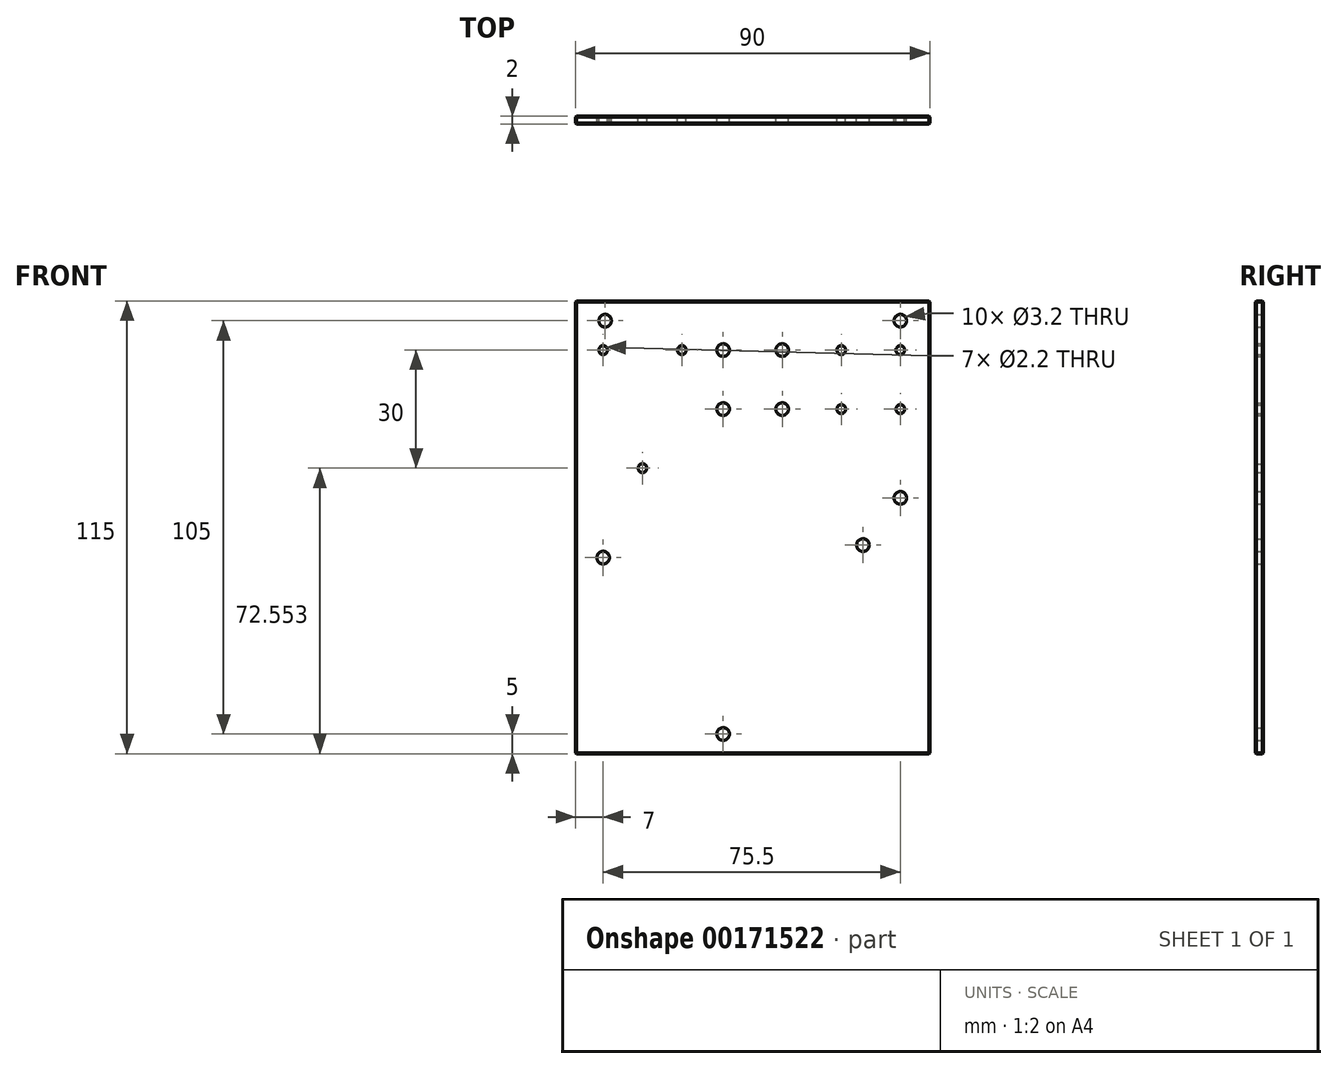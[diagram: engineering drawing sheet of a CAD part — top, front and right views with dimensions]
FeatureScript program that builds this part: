
annotation { "Feature Type Name" : "Feature", "Feature Type Description" : "" }
export const myFeature = defineFeature(function(context is Context, id is Id, definition is map)
    precondition{}
    {
        {
            var Q0;
            Q0=qCreatedBy(makeId("Front.planeOp"),FACE);
            var sketch = newSketch(context, id + "F0", { "sketchPlane" : qUnion([Q0])});
            skLineSegment(sketch, "E0.bottom", {"start": v(45, -57.5) * mm, "end": v(-45, -57.5) * mm});
            skLineSegment(sketch, "E0.top", {"start": v(45, 57.5) * mm, "end": v(-45, 57.5) * mm});
            skLineSegment(sketch, "E0.left", {"start": v(45, -57.5) * mm, "end": v(45, 57.5) * mm});
            skLineSegment(sketch, "E0.right", {"start": v(-45, -57.5) * mm, "end": v(-45, 57.5) * mm});
            skPoint(sketch, "E0.middle", {"position": v(0, 0) * mm});
            skCircle(sketch, "E1", {"center": v(-37.5, 52.5) * mm, "radius": 1.6 * mm});
            skCircle(sketch, "E2", {"center": v(37.5, 52.5) * mm, "radius": 1.6 * mm});
            skCircle(sketch, "E3", {"center": v(37.5, 7.5) * mm, "radius": 1.6 * mm});
            skCircle(sketch, "E4", {"center": v(-7.5, -52.5) * mm, "radius": 1.6 * mm});
            skCircle(sketch, "E5", {"center": v(-38, -7.7) * mm, "radius": 1.6 * mm});
            skCircle(sketch, "E6", {"center": v(28, -4.5) * mm, "radius": 1.6 * mm});
            skPoint(sketch, "E7.middle", {"position": v(30, 37.55) * mm});
            skPoint(sketch, "E8.middle", {"position": v(0, 37.55) * mm});
            skPoint(sketch, "E8.middle.positionSnap0", {"position": v(22.5, 37.55) * mm});
            skPoint(sketch, "E8.centerSnap0", {"position": v(22.5, 37.55) * mm});
            skCircle(sketch, "E9", {"center": v(-18, 45.05) * mm, "radius": 1.1 * mm});
            skCircle(sketch, "E10", {"center": v(-38, 45.05) * mm, "radius": 1.1 * mm});
            skCircle(sketch, "E11", {"center": v(-28, 15.05) * mm, "radius": 1.1 * mm});
            skCircle(sketch, "E12", {"center": v(-7.5, 45.05) * mm, "radius": 1.6 * mm});
            skCircle(sketch, "E13", {"center": v(7.5, 45.05) * mm, "radius": 1.6 * mm});
            skCircle(sketch, "E14", {"center": v(-7.5, 30.05) * mm, "radius": 1.6 * mm});
            skCircle(sketch, "E15", {"center": v(7.5, 30.05) * mm, "radius": 1.6 * mm});
            skCircle(sketch, "E16", {"center": v(22.5, 45.05) * mm, "radius": 1.1 * mm});
            skCircle(sketch, "E17", {"center": v(37.5, 45.05) * mm, "radius": 1.1 * mm});
            skCircle(sketch, "E18", {"center": v(37.5, 30.05) * mm, "radius": 1.1 * mm});
            skCircle(sketch, "E19", {"center": v(22.5, 30.05) * mm, "radius": 1.1 * mm});
            skSolve(sketch);
        }
        {
            var Q0;
            Q0=makeQuery(id+"F0.imprint","IMPRINT",FACE,{"disambiguationData":[TD([[makeQuery(id+"F0.imprint","IMPRINT",EDGE,{"derivedFrom":sQuery(id+"F0.wireOp",EDGE,"E0.bottom")}),-1.0]])]});
            extrude(context, id + "F1", {"entities" : qUnion([Q0]), "depth" : 2 * mm});
        }
        {
            var Q0;
            Q0=makeQuery(id+"F1.opExtrude","CAP_EDGE",EDGE,{"disambiguationData":[OSD([sQuery(id+"F0.wireOp",EDGE,"E0.left")])],"isStart":false});
            var Q1;
            Q1=makeQuery(id+"F1.opExtrude","CAP_EDGE",EDGE,{"disambiguationData":[OSD([sQuery(id+"F0.wireOp",EDGE,"E0.bottom")])],"isStart":false});
            var Q2;
            Q2=makeQuery(id+"F1.opExtrude","CAP_EDGE",EDGE,{"disambiguationData":[OSD([sQuery(id+"F0.wireOp",EDGE,"E0.left")])],"isStart":true});
            var Q3;
            Q3=makeQuery(id+"F1.opExtrude","CAP_EDGE",EDGE,{"disambiguationData":[OSD([sQuery(id+"F0.wireOp",EDGE,"E0.bottom")])],"isStart":true});
            var Q4;
            Q4=makeQuery(id+"F1.opExtrude","SWEPT_EDGE",EDGE,{"disambiguationData":[OSD([sQuery(id+"F0.wireOp",EDGE,"E0.bottom"),sQuery(id+"F0.wireOp",EDGE,"E0.left")])]});
            var Q5;
            Q5=makeQuery(id+"F1.opExtrude","SWEPT_EDGE",EDGE,{"disambiguationData":[OSD([sQuery(id+"F0.wireOp",EDGE,"E0.bottom"),sQuery(id+"F0.wireOp",EDGE,"E0.right")])]});
            var Q6;
            Q6=makeQuery(id+"F1.opExtrude","CAP_EDGE",EDGE,{"disambiguationData":[OSD([sQuery(id+"F0.wireOp",EDGE,"E0.right")])],"isStart":false});
            var Q7;
            Q7=makeQuery(id+"F1.opExtrude","CAP_EDGE",EDGE,{"disambiguationData":[OSD([sQuery(id+"F0.wireOp",EDGE,"E0.right")])],"isStart":true});
            var Q8;
            Q8=makeQuery(id+"F1.opExtrude","CAP_FACE",FACE,{"disambiguationData":[OSD([sQuery(id+"F0.wireOp",EDGE,"E0.bottom"),sQuery(id+"F0.wireOp",EDGE,"E0.top"),sQuery(id+"F0.wireOp",EDGE,"E0.left"),sQuery(id+"F0.wireOp",EDGE,"E0.right"),sQuery(id+"F0.wireOp",EDGE,"E1"),sQuery(id+"F0.wireOp",EDGE,"E2"),sQuery(id+"F0.wireOp",EDGE,"E3"),sQuery(id+"F0.wireOp",EDGE,"E4"),sQuery(id+"F0.wireOp",EDGE,"E5"),sQuery(id+"F0.wireOp",EDGE,"E6")])],"isStart":true});
            var Q9;
            Q9=makeQuery(id+"F1.opExtrude","CAP_EDGE",EDGE,{"disambiguationData":[OSD([sQuery(id+"F0.wireOp",EDGE,"E0.top")])],"isStart":false});
            var Q10;
            Q10=makeQuery(id+"F1.opExtrude","SWEPT_EDGE",EDGE,{"disambiguationData":[OSD([sQuery(id+"F0.wireOp",EDGE,"E0.top"),sQuery(id+"F0.wireOp",EDGE,"E0.left")])]});
            var Q11;
            Q11=makeQuery(id+"F1.opExtrude","SWEPT_EDGE",EDGE,{"disambiguationData":[OSD([sQuery(id+"F0.wireOp",EDGE,"E0.top"),sQuery(id+"F0.wireOp",EDGE,"E0.right")])]});
            chamfer(context, id + "F2", {"entities" : qUnion([Q0, Q1, Q2, Q3, Q4, Q5, Q6, Q7, Q8, Q9, Q10, Q11]), "width" : 0.2 * mm, "tangentPropagation" : true});
        }
    });
